# Revit family: Trane_TVR_Indoor_Fresh Air_4TVF0042(48)EF000AA(2nd DC)
name_source: partatom
category: Equipamento mecânico
units: mm (PartAtom-declared; Revit-internal decimal feet)

## family parameters
Com base no plano de trabalho = Não
Compartilhado = Não
Corte com vazios quando carregada = Não
Cota do conector redondo = Utilizar diâmetro
Número OmniClass = 23.75.00.00
Ponto de cálculo do ambiente = Não
Sempre na vertical = Sim
Tipo de parte = Normal
Título OmniClass = Climate Control (HVAC)

## types (2) — shared parameters
Air  Flow = 2000/1917/1833/1750/1667/1583/1500 m3/h
Condensation = air
Cooling Power Input = 480.000 W
Depth = 691  [stored 2.26706 ft]
Descrição = High efficiency air cooled
Fabricante = TRANE
Gas = R410a
Gas pipe = 15.9  [stored 0.0521654 ft]
Heating Power Input = 480.000 W
Height = 423  [stored 1.3878 ft]
Installation = Indoor installation
Liquid pipe = 9.53
Maximum Fuse Amps = 15 A
Minimum Circuit Amps = 4 A
Net Weight = 68.00 kg
Power supply = 220-240V ~50/60Hz
Series = ULTRA
URL = https://www.trane.com
Width = 1322  [stored 4.33727 ft]
clearance access behind = 600  [stored 1.9685 ft]
clearance access front = 500  [stored 1.64042 ft]
clearance access left = 600  [stored 1.9685 ft]
clearance access right = 600  [stored 1.9685 ft]

## per-type parameters (varying)
| type | Cooling Capacity | Heating Capacity |
| 4TVF0042EF000AA | 12.50 kW | 10.50 kW |
| 4TVF0048EF000AA | 14.00 kW | 12.00 kW |

note: column(s) folded — value = type name in every type: Modelo

note: [stored X ft] marks values corroborated as IEEE doubles in the binary element streams (Revit-internal decimal feet)

## geometry (parser evidence)
native form markers: Blend x4, Sweep x11
no freeform markers — native parametric forms only
